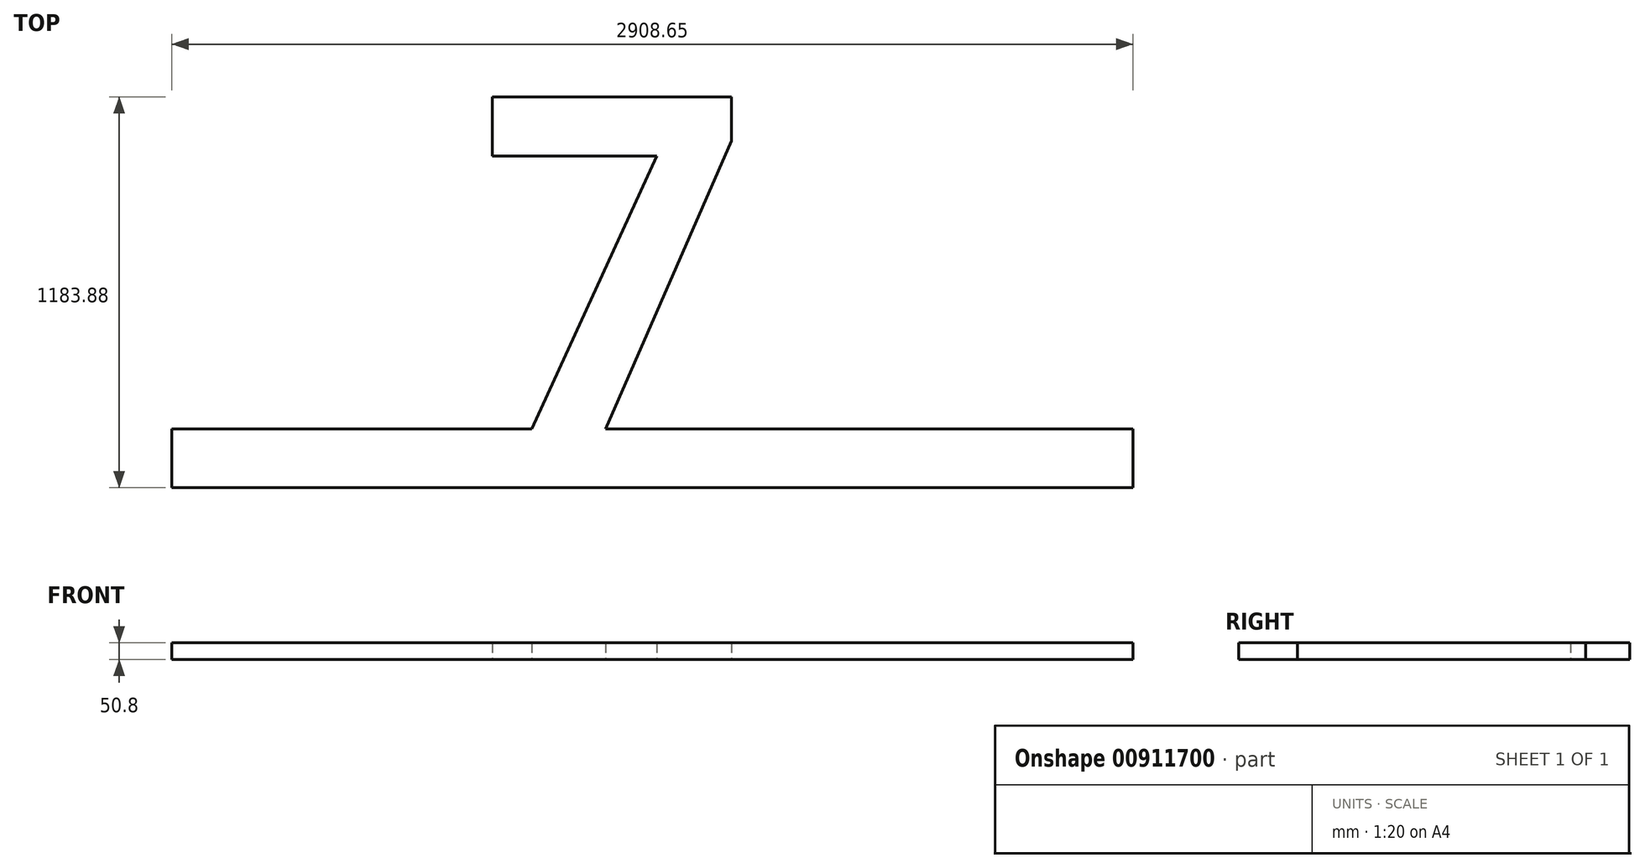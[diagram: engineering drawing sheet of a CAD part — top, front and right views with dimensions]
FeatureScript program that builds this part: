
annotation { "Feature Type Name" : "Feature", "Feature Type Description" : "" }
export const myFeature = defineFeature(function(context is Context, id is Id, definition is map)
    precondition{}
    {
        {
            var Q0;
            Q0=qCreatedBy(makeId("Top.planeOp"),FACE);
            var sketch = newSketch(context, id + "F0", { "sketchPlane" : qUnion([Q0])});
            skLineSegment(sketch, "E0.bottom", {"start": v(-275.51, -177.8) * mm, "end": v(2633.14, -177.8) * mm});
            skLineSegment(sketch, "E0.top", {"start": v(-275.51, 0) * mm, "end": v(2633.14, 0) * mm});
            skLineSegment(sketch, "E0.left", {"start": v(-275.51, -177.8) * mm, "end": v(-275.51, 0) * mm});
            skLineSegment(sketch, "E0.right", {"start": v(2633.14, -177.8) * mm, "end": v(2633.14, 0) * mm});
            skText(sketch, "E1", { "text": "17H", "fontName": "OpenSans-Bold.ttf"});
            const initialGuessF0  = {"E1": [-0.14851, 0, 1, 0, 1.016]};
            skSetInitialGuess(sketch, initialGuessF0);
            skSolve(sketch);
        }
        {
            var Q0;
            Q0=makeQuery(id+"F0.imprint","IMPRINT",FACE,{"disambiguationData":[TD([[makeQuery(id+"F0.imprint","IMPRINT",EDGE,{"derivedFrom":sQuery(id+"F0.wireOp",EDGE,"c1c0e49b-6bd2-41c1-8fb2-2985bfaaa17b.sketch_text.stroke-10")}),-1.0]])]});
            var Q1;
            {var subQ0=sQuery(id+"F0.wireOp",EDGE,"c1c0e49b-6bd2-41c1-8fb2-2985bfaaa17b.sketch_text.stroke-24");var subQ1=sQuery(id+"F0.wireOp",EDGE,"E0.top");var subQ2=makeQuery(id+"F0.imprint","INTERSECT",VERTEX,{"derivedFrom":[subQ1,subQ0]});Q1=makeQuery(id+"F0.imprint","IMPRINT",FACE,{"disambiguationData":[TD([[makeQuery(id+"F0.imprint","IMPRINT",EDGE,{"disambiguationData":[TD([[subQ2,-1.0]])],"derivedFrom":subQ1}),-1.0]])]});}
            var Q2;
            Q2=makeQuery(id+"F0.imprint","IMPRINT",FACE,{"disambiguationData":[TD([[makeQuery(id+"F0.imprint","IMPRINT",EDGE,{"derivedFrom":sQuery(id+"F0.wireOp",EDGE,"E0.bottom")}),1.0]])]});
            var Q3;
            Q3=makeQuery(id+"F0.imprint","IMPRINT",FACE,{"disambiguationData":[TD([[makeQuery(id+"F0.imprint","IMPRINT",EDGE,{"derivedFrom":sQuery(id+"F0.wireOp",EDGE,"c1c0e49b-6bd2-41c1-8fb2-2985bfaaa17b.sketch_text.stroke-0")}),-1.0]])]});
            var Q4;
            Q4=makeQuery(id+"F0.imprint","IMPRINT",FACE,{"disambiguationData":[TD([[makeQuery(id+"F0.imprint","IMPRINT",EDGE,{"derivedFrom":sQuery(id+"F0.wireOp",EDGE,"c1c0e49b-6bd2-41c1-8fb2-2985bfaaa17b.sketch_text.stroke-35")}),-1.0]])]});
            var Q5;
            Q5=makeQuery(id+"F0.imprint","IMPRINT",FACE,{"disambiguationData":[TD([[makeQuery(id+"F0.imprint","IMPRINT",EDGE,{"derivedFrom":sQuery(id+"F0.wireOp",EDGE,"E1.sketch_text.stroke-10")}),-1.0]])]});
            var Q6;
            Q6=makeQuery(id+"F0.imprint","IMPRINT",FACE,{"disambiguationData":[TD([[makeQuery(id+"F0.imprint","IMPRINT",EDGE,{"derivedFrom":sQuery(id+"F0.wireOp",EDGE,"E1.sketch_text.stroke-17")}),-1.0]])]});
            var Q7;
            Q7=makeQuery(id+"F0.imprint","IMPRINT",FACE,{"disambiguationData":[TD([[makeQuery(id+"F0.imprint","IMPRINT",EDGE,{"derivedFrom":sQuery(id+"F0.wireOp",EDGE,"E1.sketch_text.stroke-0")}),-1.0]])]});
            extrude(context, id + "F1", {"entities" : qUnion([Q0, Q1, Q2, Q3, Q4, Q5, Q6, Q7]), "depth" : 50.8 * mm, "offsetDistance" : 25.4 * mm});
        }
    });
